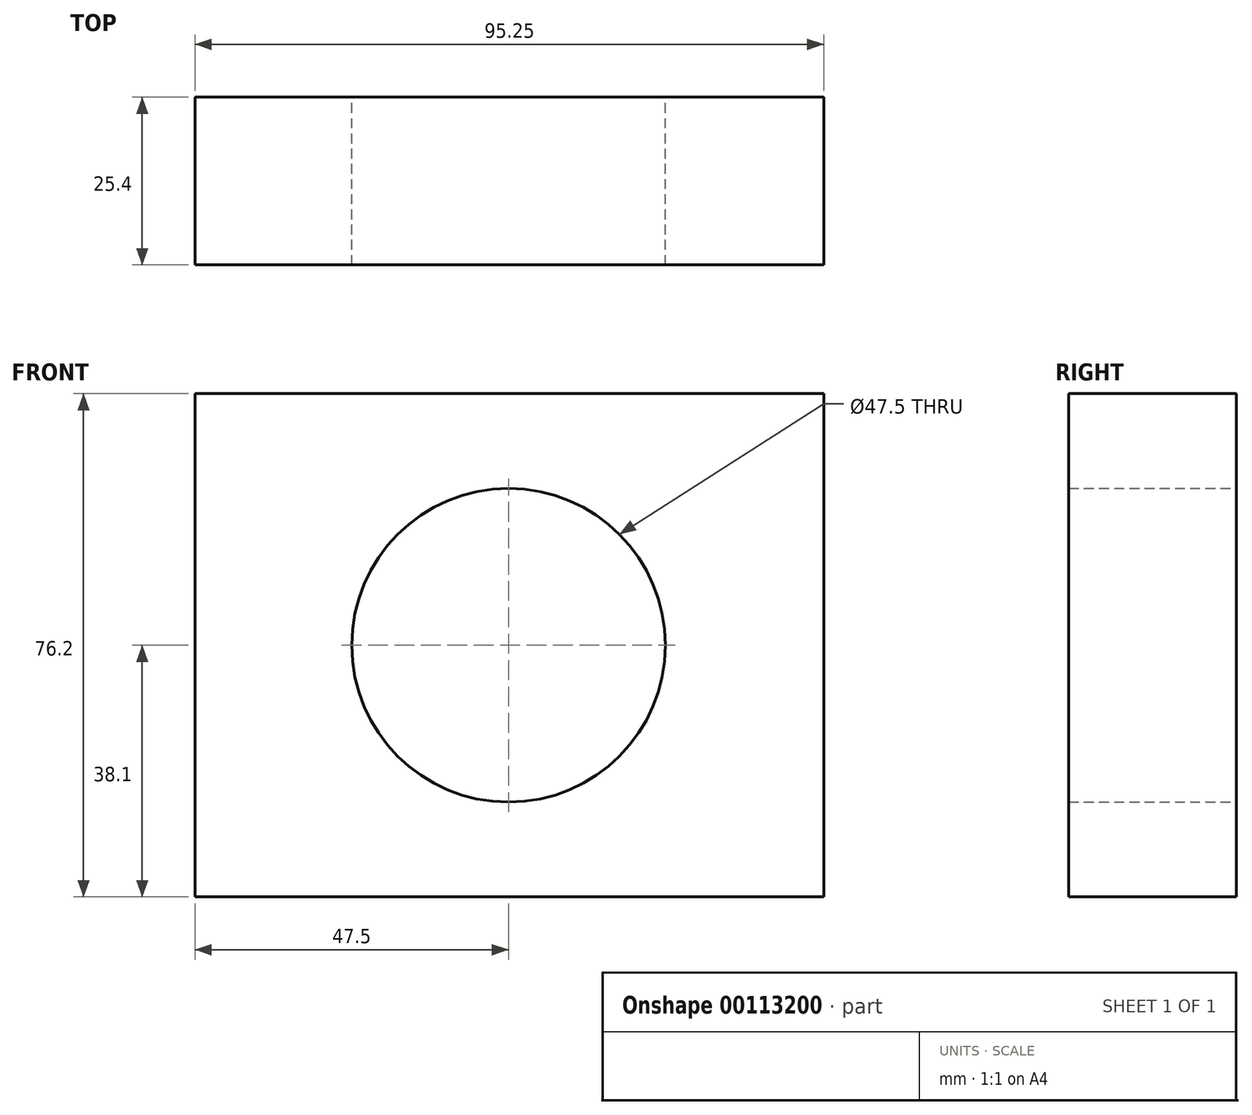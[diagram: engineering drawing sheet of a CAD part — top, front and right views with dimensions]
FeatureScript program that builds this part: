
annotation { "Feature Type Name" : "Feature", "Feature Type Description" : "" }
export const myFeature = defineFeature(function(context is Context, id is Id, definition is map)
    precondition{}
    {
        {
            var Q0;
            Q0=qCreatedBy(makeId("Front.planeOp"),FACE);
            var sketch = newSketch(context, id + "F0", { "sketchPlane" : qUnion([Q0])});
            skLineSegment(sketch, "E0.bottom", {"start": v(-47.5, 38.1) * mm, "end": v(47.75, 38.1) * mm});
            skLineSegment(sketch, "E0.top", {"start": v(-47.5, -38.1) * mm, "end": v(47.75, -38.1) * mm});
            skLineSegment(sketch, "E0.left", {"start": v(-47.5, 38.1) * mm, "end": v(-47.5, -38.1) * mm});
            skLineSegment(sketch, "E0.right", {"start": v(47.75, 38.1) * mm, "end": v(47.75, -38.1) * mm});
            skCircle(sketch, "E1", {"center": v(0, 0) * mm, "radius": 23.75 * mm});
            skSolve(sketch);
        }
        {
            var Q0;
            Q0=makeQuery(id+"F0.imprint","IMPRINT",FACE,{"disambiguationData":[TD([[makeQuery(id+"F0.imprint","IMPRINT",EDGE,{"derivedFrom":sQuery(id+"F0.wireOp",EDGE,"E0.bottom")}),-1.0]])]});
            extrude(context, id + "F1", {"entities" : qUnion([Q0]), "depth" : 25.4 * mm});
        }
    });
